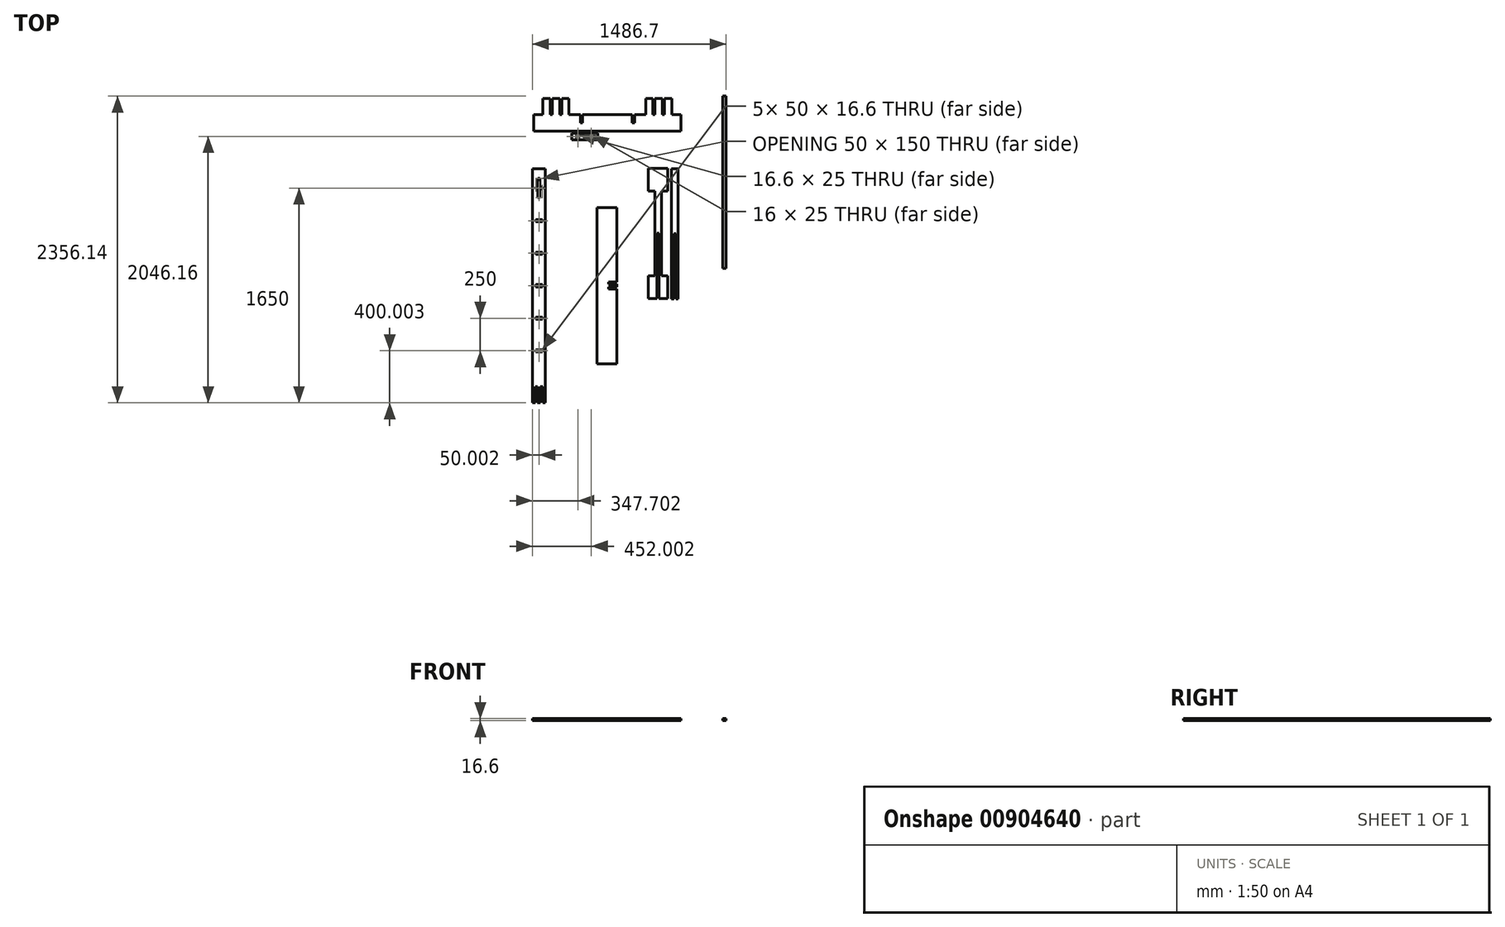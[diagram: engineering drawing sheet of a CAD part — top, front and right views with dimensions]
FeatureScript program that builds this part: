
annotation { "Feature Type Name" : "Feature", "Feature Type Description" : "" }
export const myFeature = defineFeature(function(context is Context, id is Id, definition is map)
    precondition{}
    {
        {
            assignVariable(context, id + "F0", {"name" : "s", "anyValue" : 16.6});
        }
        {
            var Q0;
            Q0=qCreatedBy(makeId("Top.planeOp"),FACE);
            var sketch = newSketch(context, id + "F1", { "sketchPlane" : qUnion([Q0])});
            skLineSegment(sketch, "E0.bottom", {"start": v(575, 24) * mm, "end": v(-575, 24) * mm});
            skLineSegment(sketch, "E0.top", {"start": v(575, 2324) * mm, "end": v(-575, 2324) * mm});
            skLineSegment(sketch, "E0.left", {"start": v(575, 24) * mm, "end": v(575, 2324) * mm});
            skLineSegment(sketch, "E0.right", {"start": v(-575, 24) * mm, "end": v(-575, 2324) * mm});
            skPoint(sketch, "E0.middle", {"position": v(0, 1174) * mm});
            skLineSegment(sketch, "E1.bottom", {"start": v(1816.08, 2142.02) * mm, "end": v(1916.08, 2142.02) * mm});
            skLineSegment(sketch, "E1.top", {"start": v(1816.08, 342.02) * mm, "end": v(1838.35, 342.02) * mm});
            skLineSegment(sketch, "E1.left", {"start": v(1816.08, 2142.02) * mm, "end": v(1816.08, 342.02) * mm});
            skLineSegment(sketch, "E1.right", {"start": v(1916.08, 2142.02) * mm, "end": v(1916.08, 342.02) * mm});
            skPoint(sketch, "E1.middle", {"position": v(1866.08, 1242.02) * mm});
            skLineSegment(sketch, "E2.top", {"start": v(1838.35, 467.02) * mm, "end": v(1854.95, 467.02) * mm});
            skLineSegment(sketch, "E2.left", {"start": v(1838.35, 342.02) * mm, "end": v(1838.35, 467.02) * mm});
            skLineSegment(sketch, "E2.right", {"start": v(1854.95, 342.02) * mm, "end": v(1854.95, 467.02) * mm});
            skLineSegment(sketch, "E3.top", {"start": v(1877.22, 467.02) * mm, "end": v(1893.82, 467.02) * mm});
            skLineSegment(sketch, "E3.left", {"start": v(1877.22, 342.02) * mm, "end": v(1877.22, 467.02) * mm});
            skLineSegment(sketch, "E3.right", {"start": v(1893.82, 342.02) * mm, "end": v(1893.82, 467.02) * mm});
            skLineSegment(sketch, "E4.trimOffspring", {"start": v(1854.95, 342.02) * mm, "end": v(1877.22, 342.02) * mm});
            skLineSegment(sketch, "E5.trimOffspring", {"start": v(1893.82, 342.02) * mm, "end": v(1916.08, 342.02) * mm});
            skLineSegment(sketch, "E6.bottom", {"start": v(1891.08, 1233.72) * mm, "end": v(1841.08, 1233.72) * mm});
            skLineSegment(sketch, "E6.top", {"start": v(1891.08, 1250.32) * mm, "end": v(1841.08, 1250.32) * mm});
            skLineSegment(sketch, "E6.left", {"start": v(1891.08, 1233.72) * mm, "end": v(1891.08, 1250.32) * mm});
            skLineSegment(sketch, "E6.right", {"start": v(1841.08, 1233.72) * mm, "end": v(1841.08, 1250.32) * mm});
            skLineSegment(sketch, "E7.0.1.0", {"start": v(1891.08, 1500.32) * mm, "end": v(1841.08, 1500.32) * mm});
            skLineSegment(sketch, "E7.0.1.1", {"start": v(1891.08, 1483.72) * mm, "end": v(1891.08, 1500.32) * mm});
            skPoint(sketch, "E7.0.1.2", {"position": v(1866.08, 1492.02) * mm});
            skLineSegment(sketch, "E7.0.1.3", {"start": v(1891.08, 1483.72) * mm, "end": v(1841.08, 1483.72) * mm});
            skLineSegment(sketch, "E7.0.1.4", {"start": v(1841.08, 1483.72) * mm, "end": v(1841.08, 1500.32) * mm});
            skPoint(sketch, "E7.0.1.5", {"position": v(1866.08, 1492.02) * mm});
            skLineSegment(sketch, "E7.direction1", {"start": v(1841.08, 1233.72) * mm, "end": v(1866.08, 1233.72) * mm, "construction": true});
            skLineSegment(sketch, "E7.direction2", {"start": v(1841.08, 1233.72) * mm, "end": v(1841.08, 1483.72) * mm, "construction": true});
            skLineSegment(sketch, "E8.0.0.2", {"start": v(1891.08, 1750.32) * mm, "end": v(1841.08, 1750.32) * mm});
            skLineSegment(sketch, "E8.3.0.2", {"start": v(1891.08, 1733.72) * mm, "end": v(1891.08, 1750.32) * mm});
            skPoint(sketch, "E8.6.0.2", {"position": v(1866.08, 1742.02) * mm});
            skLineSegment(sketch, "E8.7.0.2", {"start": v(1891.08, 1733.72) * mm, "end": v(1841.08, 1733.72) * mm});
            skLineSegment(sketch, "E8.10.0.2", {"start": v(1841.08, 1733.72) * mm, "end": v(1841.08, 1750.32) * mm});
            skPoint(sketch, "E8.13.0.2", {"position": v(1866.08, 1742.02) * mm});
            skLineSegment(sketch, "E8.0.0.3", {"start": v(1891.08, 2000.32) * mm, "end": v(1874.38, 2000.32) * mm});
            skLineSegment(sketch, "E8.3.0.3", {"start": v(1891.08, 1983.72) * mm, "end": v(1891.08, 2000.32) * mm});
            skPoint(sketch, "E8.6.0.3", {"position": v(1866.08, 1992.02) * mm});
            skLineSegment(sketch, "E8.7.0.3", {"start": v(1891.08, 1983.72) * mm, "end": v(1874.38, 1983.72) * mm});
            skLineSegment(sketch, "E8.10.0.3", {"start": v(1841.08, 1983.72) * mm, "end": v(1841.08, 2000.32) * mm});
            skPoint(sketch, "E8.13.0.3", {"position": v(1866.08, 1992.02) * mm});
            skLineSegment(sketch, "E9.0.1.0", {"start": v(1891.08, 983.72) * mm, "end": v(1841.08, 983.72) * mm});
            skPoint(sketch, "E9.0.1.1", {"position": v(1866.08, 992.02) * mm});
            skLineSegment(sketch, "E9.0.1.2", {"start": v(1891.08, 1000.32) * mm, "end": v(1841.08, 1000.32) * mm});
            skLineSegment(sketch, "E9.0.1.3", {"start": v(1841.08, 983.72) * mm, "end": v(1841.08, 1000.32) * mm});
            skLineSegment(sketch, "E9.0.1.4", {"start": v(1841.08, 983.72) * mm, "end": v(1866.08, 983.72) * mm, "construction": true});
            skLineSegment(sketch, "E9.0.1.5", {"start": v(1891.08, 983.72) * mm, "end": v(1891.08, 1000.32) * mm});
            skPoint(sketch, "E9.0.1.6", {"position": v(1866.08, 992.02) * mm});
            skLineSegment(sketch, "E9.direction2", {"start": v(1841.08, 1233.72) * mm, "end": v(1841.08, 983.72) * mm, "construction": true});
            skLineSegment(sketch, "E10.0.0.2", {"start": v(1891.08, 733.72) * mm, "end": v(1841.08, 733.72) * mm});
            skPoint(sketch, "E10.3.0.2", {"position": v(1866.08, 742.02) * mm});
            skLineSegment(sketch, "E10.4.0.2", {"start": v(1891.08, 750.32) * mm, "end": v(1841.08, 750.32) * mm});
            skLineSegment(sketch, "E10.7.0.2", {"start": v(1841.08, 733.72) * mm, "end": v(1841.08, 750.32) * mm});
            skLineSegment(sketch, "E10.10.0.2", {"start": v(1841.08, 733.72) * mm, "end": v(1866.08, 733.72) * mm, "construction": true});
            skLineSegment(sketch, "E10.13.0.2", {"start": v(1891.08, 733.72) * mm, "end": v(1891.08, 750.32) * mm});
            skPoint(sketch, "E10.16.0.2", {"position": v(1866.08, 742.02) * mm});
            skPoint(sketch, "E11.1.0.0", {"position": v(1991.08, 1242.02) * mm});
            skPoint(sketch, "E11.1.0.1", {"position": v(1991.08, 742.02) * mm});
            skPoint(sketch, "E11.1.0.2", {"position": v(1991.08, 1742.02) * mm});
            skLineSegment(sketch, "E11.1.0.3", {"start": v(1941.08, 2142.02) * mm, "end": v(1941.08, 342.02) * mm});
            skPoint(sketch, "E11.1.0.4", {"position": v(1991.08, 1492.02) * mm});
            skPoint(sketch, "E11.1.0.5", {"position": v(1991.08, 1992.02) * mm});
            skPoint(sketch, "E11.1.0.6", {"position": v(1991.08, 992.02) * mm});
            skLineSegment(sketch, "E11.1.0.7", {"start": v(1966.08, 1233.72) * mm, "end": v(1966.08, 1483.72) * mm, "construction": true});
            skLineSegment(sketch, "E11.1.0.8", {"start": v(2041.08, 2142.02) * mm, "end": v(2041.08, 342.02) * mm});
            skLineSegment(sketch, "E11.1.0.9", {"start": v(1941.08, 2142.02) * mm, "end": v(2041.08, 2142.02) * mm});
            skPoint(sketch, "E11.1.0.10", {"position": v(1991.08, 1992.02) * mm});
            skLineSegment(sketch, "E11.1.0.11", {"start": v(1966.08, 1233.72) * mm, "end": v(1966.08, 983.72) * mm, "construction": true});
            skPoint(sketch, "E11.1.0.12", {"position": v(1991.08, 1242.02) * mm});
            skPoint(sketch, "E11.1.0.13", {"position": v(1991.08, 1492.02) * mm});
            skPoint(sketch, "E11.1.0.14", {"position": v(1991.08, 992.02) * mm});
            skLineSegment(sketch, "E11.1.0.15", {"start": v(2018.82, 342.02) * mm, "end": v(2018.82, 467.02) * mm});
            skLineSegment(sketch, "E11.1.0.16", {"start": v(1979.95, 342.02) * mm, "end": v(1979.95, 467.02) * mm});
            skPoint(sketch, "E11.1.0.17", {"position": v(1991.08, 1742.02) * mm});
            skLineSegment(sketch, "E11.1.0.18", {"start": v(1963.35, 342.02) * mm, "end": v(1963.35, 467.02) * mm});
            skLineSegment(sketch, "E11.1.0.19", {"start": v(2002.22, 342.02) * mm, "end": v(2002.22, 467.02) * mm});
            skPoint(sketch, "E11.1.0.20", {"position": v(1991.08, 742.02) * mm});
            skLineSegment(sketch, "E11.1.0.21", {"start": v(2016.08, 1500.32) * mm, "end": v(1966.08, 1500.32) * mm});
            skLineSegment(sketch, "E11.1.0.22", {"start": v(2016.08, 2000.32) * mm, "end": v(1966.08, 2000.32) * mm});
            skLineSegment(sketch, "E11.1.0.23", {"start": v(2016.08, 1983.72) * mm, "end": v(1966.08, 1983.72) * mm});
            skLineSegment(sketch, "E11.1.0.24", {"start": v(2016.08, 1483.72) * mm, "end": v(1966.08, 1483.72) * mm});
            skLineSegment(sketch, "E11.1.0.25", {"start": v(2016.08, 1483.72) * mm, "end": v(2016.08, 1500.32) * mm});
            skLineSegment(sketch, "E11.1.0.26", {"start": v(2016.08, 1983.72) * mm, "end": v(2016.08, 2000.32) * mm});
            skLineSegment(sketch, "E11.1.0.27", {"start": v(1966.08, 1983.72) * mm, "end": v(1966.08, 2000.32) * mm});
            skLineSegment(sketch, "E11.1.0.28", {"start": v(2016.08, 1733.72) * mm, "end": v(2016.08, 1750.32) * mm});
            skLineSegment(sketch, "E11.1.0.29", {"start": v(1941.08, 342.02) * mm, "end": v(1963.35, 342.02) * mm});
            skLineSegment(sketch, "E11.1.0.30", {"start": v(1979.95, 342.02) * mm, "end": v(2002.22, 342.02) * mm});
            skLineSegment(sketch, "E11.1.0.31", {"start": v(2016.08, 983.72) * mm, "end": v(1966.08, 983.72) * mm});
            skLineSegment(sketch, "E11.1.0.32", {"start": v(2016.08, 1750.32) * mm, "end": v(1966.08, 1750.32) * mm});
            skLineSegment(sketch, "E11.1.0.33", {"start": v(1963.35, 467.02) * mm, "end": v(1979.95, 467.02) * mm});
            skLineSegment(sketch, "E11.1.0.34", {"start": v(2016.08, 1000.32) * mm, "end": v(1966.08, 1000.32) * mm});
            skLineSegment(sketch, "E11.1.0.35", {"start": v(2016.08, 983.72) * mm, "end": v(2016.08, 1000.32) * mm});
            skLineSegment(sketch, "E11.1.0.36", {"start": v(1966.08, 1483.72) * mm, "end": v(1966.08, 1500.32) * mm});
            skLineSegment(sketch, "E11.1.0.37", {"start": v(2018.82, 342.02) * mm, "end": v(2041.08, 342.02) * mm});
            skLineSegment(sketch, "E11.1.0.38", {"start": v(1966.08, 733.72) * mm, "end": v(1966.08, 750.32) * mm});
            skLineSegment(sketch, "E11.1.0.39", {"start": v(2002.22, 467.02) * mm, "end": v(2018.82, 467.02) * mm});
            skLineSegment(sketch, "E11.1.0.40", {"start": v(2016.08, 1733.72) * mm, "end": v(1966.08, 1733.72) * mm});
            skLineSegment(sketch, "E11.1.0.41", {"start": v(1966.08, 733.72) * mm, "end": v(1991.08, 733.72) * mm, "construction": true});
            skLineSegment(sketch, "E11.1.0.42", {"start": v(2016.08, 1233.72) * mm, "end": v(2016.08, 1250.32) * mm});
            skLineSegment(sketch, "E11.1.0.43", {"start": v(1966.08, 983.72) * mm, "end": v(1966.08, 1000.32) * mm});
            skLineSegment(sketch, "E11.1.0.44", {"start": v(1966.08, 1733.72) * mm, "end": v(1966.08, 1750.32) * mm});
            skLineSegment(sketch, "E11.1.0.45", {"start": v(1966.08, 983.72) * mm, "end": v(1991.08, 983.72) * mm, "construction": true});
            skLineSegment(sketch, "E11.1.0.46", {"start": v(2016.08, 733.72) * mm, "end": v(1966.08, 733.72) * mm});
            skLineSegment(sketch, "E11.1.0.47", {"start": v(2016.08, 1233.72) * mm, "end": v(1966.08, 1233.72) * mm});
            skLineSegment(sketch, "E11.1.0.48", {"start": v(2016.08, 733.72) * mm, "end": v(2016.08, 750.32) * mm});
            skLineSegment(sketch, "E11.1.0.49", {"start": v(2016.08, 750.32) * mm, "end": v(1966.08, 750.32) * mm});
            skLineSegment(sketch, "E11.1.0.50", {"start": v(2016.08, 1250.32) * mm, "end": v(1966.08, 1250.32) * mm});
            skLineSegment(sketch, "E11.1.0.51", {"start": v(1966.08, 1233.72) * mm, "end": v(1966.08, 1250.32) * mm});
            skLineSegment(sketch, "E11.1.0.52", {"start": v(1966.08, 1233.72) * mm, "end": v(1991.08, 1233.72) * mm, "construction": true});
            skLineSegment(sketch, "E11.1.0.53", {"start": v(1966.08, 1233.72) * mm, "end": v(1991.08, 1233.72) * mm, "construction": true});
            skPoint(sketch, "E11.2.0.0", {"position": v(2116.08, 1242.02) * mm});
            skPoint(sketch, "E11.2.0.1", {"position": v(2116.08, 742.02) * mm});
            skPoint(sketch, "E11.2.0.2", {"position": v(2116.08, 1742.02) * mm});
            skLineSegment(sketch, "E11.2.0.3", {"start": v(2066.08, 2142.02) * mm, "end": v(2066.08, 342.02) * mm});
            skPoint(sketch, "E11.2.0.4", {"position": v(2116.08, 1492.02) * mm});
            skPoint(sketch, "E11.2.0.5", {"position": v(2116.08, 1992.02) * mm});
            skPoint(sketch, "E11.2.0.6", {"position": v(2116.08, 992.02) * mm});
            skLineSegment(sketch, "E11.2.0.7", {"start": v(2091.08, 1233.72) * mm, "end": v(2091.08, 1483.72) * mm, "construction": true});
            skLineSegment(sketch, "E11.2.0.8", {"start": v(2166.08, 2142.02) * mm, "end": v(2166.08, 342.02) * mm});
            skLineSegment(sketch, "E11.2.0.9", {"start": v(2066.08, 2142.02) * mm, "end": v(2166.08, 2142.02) * mm});
            skPoint(sketch, "E11.2.0.10", {"position": v(2116.08, 1992.02) * mm});
            skLineSegment(sketch, "E11.2.0.11", {"start": v(2091.08, 1233.72) * mm, "end": v(2091.08, 983.72) * mm, "construction": true});
            skPoint(sketch, "E11.2.0.12", {"position": v(2116.08, 1242.02) * mm});
            skPoint(sketch, "E11.2.0.13", {"position": v(2116.08, 1492.02) * mm});
            skPoint(sketch, "E11.2.0.14", {"position": v(2116.08, 992.02) * mm});
            skLineSegment(sketch, "E11.2.0.15", {"start": v(2143.82, 342.02) * mm, "end": v(2143.82, 467.02) * mm});
            skLineSegment(sketch, "E11.2.0.16", {"start": v(2104.95, 342.02) * mm, "end": v(2104.95, 467.02) * mm});
            skPoint(sketch, "E11.2.0.17", {"position": v(2116.08, 1742.02) * mm});
            skLineSegment(sketch, "E11.2.0.18", {"start": v(2088.35, 342.02) * mm, "end": v(2088.35, 467.02) * mm});
            skLineSegment(sketch, "E11.2.0.19", {"start": v(2127.22, 342.02) * mm, "end": v(2127.22, 467.02) * mm});
            skPoint(sketch, "E11.2.0.20", {"position": v(2116.08, 742.02) * mm});
            skLineSegment(sketch, "E11.2.0.21", {"start": v(2141.08, 1500.32) * mm, "end": v(2091.08, 1500.32) * mm});
            skLineSegment(sketch, "E11.2.0.22", {"start": v(2141.08, 2000.32) * mm, "end": v(2091.08, 2000.32) * mm});
            skLineSegment(sketch, "E11.2.0.23", {"start": v(2141.08, 1983.72) * mm, "end": v(2091.08, 1983.72) * mm});
            skLineSegment(sketch, "E11.2.0.24", {"start": v(2141.08, 1483.72) * mm, "end": v(2091.08, 1483.72) * mm});
            skLineSegment(sketch, "E11.2.0.25", {"start": v(2141.08, 1483.72) * mm, "end": v(2141.08, 1500.32) * mm});
            skLineSegment(sketch, "E11.2.0.26", {"start": v(2141.08, 1983.72) * mm, "end": v(2141.08, 2000.32) * mm});
            skLineSegment(sketch, "E11.2.0.27", {"start": v(2091.08, 1983.72) * mm, "end": v(2091.08, 2000.32) * mm});
            skLineSegment(sketch, "E11.2.0.28", {"start": v(2141.08, 1733.72) * mm, "end": v(2141.08, 1750.32) * mm});
            skLineSegment(sketch, "E11.2.0.29", {"start": v(2066.08, 342.02) * mm, "end": v(2088.35, 342.02) * mm});
            skLineSegment(sketch, "E11.2.0.30", {"start": v(2104.95, 342.02) * mm, "end": v(2127.22, 342.02) * mm});
            skLineSegment(sketch, "E11.2.0.31", {"start": v(2141.08, 983.72) * mm, "end": v(2091.08, 983.72) * mm});
            skLineSegment(sketch, "E11.2.0.32", {"start": v(2141.08, 1750.32) * mm, "end": v(2091.08, 1750.32) * mm});
            skLineSegment(sketch, "E11.2.0.33", {"start": v(2088.35, 467.02) * mm, "end": v(2104.95, 467.02) * mm});
            skLineSegment(sketch, "E11.2.0.34", {"start": v(2141.08, 1000.32) * mm, "end": v(2091.08, 1000.32) * mm});
            skLineSegment(sketch, "E11.2.0.35", {"start": v(2141.08, 983.72) * mm, "end": v(2141.08, 1000.32) * mm});
            skLineSegment(sketch, "E11.2.0.36", {"start": v(2091.08, 1483.72) * mm, "end": v(2091.08, 1500.32) * mm});
            skLineSegment(sketch, "E11.2.0.37", {"start": v(2143.82, 342.02) * mm, "end": v(2166.08, 342.02) * mm});
            skLineSegment(sketch, "E11.2.0.38", {"start": v(2091.08, 733.72) * mm, "end": v(2091.08, 750.32) * mm});
            skLineSegment(sketch, "E11.2.0.39", {"start": v(2127.22, 467.02) * mm, "end": v(2143.82, 467.02) * mm});
            skLineSegment(sketch, "E11.2.0.40", {"start": v(2141.08, 1733.72) * mm, "end": v(2091.08, 1733.72) * mm});
            skLineSegment(sketch, "E11.2.0.41", {"start": v(2091.08, 733.72) * mm, "end": v(2116.08, 733.72) * mm, "construction": true});
            skLineSegment(sketch, "E11.2.0.42", {"start": v(2141.08, 1233.72) * mm, "end": v(2141.08, 1250.32) * mm});
            skLineSegment(sketch, "E11.2.0.43", {"start": v(2091.08, 983.72) * mm, "end": v(2091.08, 1000.32) * mm});
            skLineSegment(sketch, "E11.2.0.44", {"start": v(2091.08, 1733.72) * mm, "end": v(2091.08, 1750.32) * mm});
            skLineSegment(sketch, "E11.2.0.45", {"start": v(2091.08, 983.72) * mm, "end": v(2116.08, 983.72) * mm, "construction": true});
            skLineSegment(sketch, "E11.2.0.46", {"start": v(2141.08, 733.72) * mm, "end": v(2091.08, 733.72) * mm});
            skLineSegment(sketch, "E11.2.0.47", {"start": v(2141.08, 1233.72) * mm, "end": v(2091.08, 1233.72) * mm});
            skLineSegment(sketch, "E11.2.0.48", {"start": v(2141.08, 733.72) * mm, "end": v(2141.08, 750.32) * mm});
            skLineSegment(sketch, "E11.2.0.49", {"start": v(2141.08, 750.32) * mm, "end": v(2091.08, 750.32) * mm});
            skLineSegment(sketch, "E11.2.0.50", {"start": v(2141.08, 1250.32) * mm, "end": v(2091.08, 1250.32) * mm});
            skLineSegment(sketch, "E11.2.0.51", {"start": v(2091.08, 1233.72) * mm, "end": v(2091.08, 1250.32) * mm});
            skLineSegment(sketch, "E11.2.0.52", {"start": v(2091.08, 1233.72) * mm, "end": v(2116.08, 1233.72) * mm, "construction": true});
            skLineSegment(sketch, "E11.2.0.53", {"start": v(2091.08, 1233.72) * mm, "end": v(2116.08, 1233.72) * mm, "construction": true});
            skLineSegment(sketch, "E11.direction1", {"start": v(1816.08, 342.02) * mm, "end": v(1941.08, 342.02) * mm, "construction": true});
            skPoint(sketch, "E12.0.3.0", {"position": v(2241.08, 1242.02) * mm});
            skPoint(sketch, "E12.1.3.0", {"position": v(2241.08, 742.02) * mm});
            skPoint(sketch, "E12.2.3.0", {"position": v(2241.08, 1742.02) * mm});
            skLineSegment(sketch, "E12.3.3.0", {"start": v(2191.08, 2142.02) * mm, "end": v(2191.08, 342.02) * mm});
            skPoint(sketch, "E12.6.3.0", {"position": v(2241.08, 1492.02) * mm});
            skPoint(sketch, "E12.7.3.0", {"position": v(2241.08, 1992.02) * mm});
            skPoint(sketch, "E12.8.3.0", {"position": v(2241.08, 992.02) * mm});
            skLineSegment(sketch, "E12.9.3.0", {"start": v(2216.08, 1233.72) * mm, "end": v(2216.08, 1483.72) * mm, "construction": true});
            skLineSegment(sketch, "E12.12.3.0", {"start": v(2291.08, 2142.02) * mm, "end": v(2291.08, 342.02) * mm});
            skLineSegment(sketch, "E12.15.3.0", {"start": v(2191.08, 2142.02) * mm, "end": v(2291.08, 2142.02) * mm});
            skPoint(sketch, "E12.18.3.0", {"position": v(2241.08, 1992.02) * mm});
            skLineSegment(sketch, "E12.19.3.0", {"start": v(2216.08, 1233.72) * mm, "end": v(2216.08, 983.72) * mm, "construction": true});
            skPoint(sketch, "E12.22.3.0", {"position": v(2241.08, 1242.02) * mm});
            skPoint(sketch, "E12.23.3.0", {"position": v(2241.08, 1492.02) * mm});
            skPoint(sketch, "E12.24.3.0", {"position": v(2241.08, 992.02) * mm});
            skLineSegment(sketch, "E12.25.3.0", {"start": v(2268.82, 342.02) * mm, "end": v(2268.82, 467.02) * mm});
            skLineSegment(sketch, "E12.28.3.0", {"start": v(2229.95, 342.02) * mm, "end": v(2229.95, 467.02) * mm});
            skPoint(sketch, "E12.31.3.0", {"position": v(2241.08, 1742.02) * mm});
            skLineSegment(sketch, "E12.32.3.0", {"start": v(2213.35, 342.02) * mm, "end": v(2213.35, 467.02) * mm});
            skLineSegment(sketch, "E12.35.3.0", {"start": v(2252.22, 342.02) * mm, "end": v(2252.22, 467.02) * mm});
            skPoint(sketch, "E12.38.3.0", {"position": v(2241.08, 742.02) * mm});
            skLineSegment(sketch, "E12.39.3.0", {"start": v(2266.08, 1500.32) * mm, "end": v(2216.08, 1500.32) * mm});
            skLineSegment(sketch, "E12.42.3.0", {"start": v(2266.08, 2000.32) * mm, "end": v(2216.08, 2000.32) * mm});
            skLineSegment(sketch, "E12.45.3.0", {"start": v(2266.08, 1983.72) * mm, "end": v(2216.08, 1983.72) * mm});
            skLineSegment(sketch, "E12.48.3.0", {"start": v(2266.08, 1483.72) * mm, "end": v(2216.08, 1483.72) * mm});
            skLineSegment(sketch, "E12.51.3.0", {"start": v(2266.08, 1483.72) * mm, "end": v(2266.08, 1500.32) * mm});
            skLineSegment(sketch, "E12.54.3.0", {"start": v(2266.08, 1983.72) * mm, "end": v(2266.08, 2000.32) * mm});
            skLineSegment(sketch, "E12.57.3.0", {"start": v(2216.08, 1983.72) * mm, "end": v(2216.08, 2000.32) * mm});
            skLineSegment(sketch, "E12.60.3.0", {"start": v(2266.08, 1733.72) * mm, "end": v(2266.08, 1750.32) * mm});
            skLineSegment(sketch, "E12.63.3.0", {"start": v(2191.08, 342.02) * mm, "end": v(2213.35, 342.02) * mm});
            skLineSegment(sketch, "E12.66.3.0", {"start": v(2229.95, 342.02) * mm, "end": v(2252.22, 342.02) * mm});
            skLineSegment(sketch, "E12.69.3.0", {"start": v(2266.08, 983.72) * mm, "end": v(2216.08, 983.72) * mm});
            skLineSegment(sketch, "E12.72.3.0", {"start": v(2266.08, 1750.32) * mm, "end": v(2216.08, 1750.32) * mm});
            skLineSegment(sketch, "E12.75.3.0", {"start": v(2213.35, 467.02) * mm, "end": v(2229.95, 467.02) * mm});
            skLineSegment(sketch, "E12.78.3.0", {"start": v(2266.08, 1000.32) * mm, "end": v(2216.08, 1000.32) * mm});
            skLineSegment(sketch, "E12.81.3.0", {"start": v(2266.08, 983.72) * mm, "end": v(2266.08, 1000.32) * mm});
            skLineSegment(sketch, "E12.84.3.0", {"start": v(2216.08, 1483.72) * mm, "end": v(2216.08, 1500.32) * mm});
            skLineSegment(sketch, "E12.87.3.0", {"start": v(2268.82, 342.02) * mm, "end": v(2291.08, 342.02) * mm});
            skLineSegment(sketch, "E12.90.3.0", {"start": v(2216.08, 733.72) * mm, "end": v(2216.08, 750.32) * mm});
            skLineSegment(sketch, "E12.93.3.0", {"start": v(2252.22, 467.02) * mm, "end": v(2268.82, 467.02) * mm});
            skLineSegment(sketch, "E12.96.3.0", {"start": v(2266.08, 1733.72) * mm, "end": v(2216.08, 1733.72) * mm});
            skLineSegment(sketch, "E12.99.3.0", {"start": v(2216.08, 733.72) * mm, "end": v(2241.08, 733.72) * mm, "construction": true});
            skLineSegment(sketch, "E12.102.3.0", {"start": v(2266.08, 1233.72) * mm, "end": v(2266.08, 1250.32) * mm});
            skLineSegment(sketch, "E12.105.3.0", {"start": v(2216.08, 983.72) * mm, "end": v(2216.08, 1000.32) * mm});
            skLineSegment(sketch, "E12.108.3.0", {"start": v(2216.08, 1733.72) * mm, "end": v(2216.08, 1750.32) * mm});
            skLineSegment(sketch, "E12.111.3.0", {"start": v(2216.08, 983.72) * mm, "end": v(2241.08, 983.72) * mm, "construction": true});
            skLineSegment(sketch, "E12.114.3.0", {"start": v(2266.08, 733.72) * mm, "end": v(2216.08, 733.72) * mm});
            skLineSegment(sketch, "E12.117.3.0", {"start": v(2266.08, 1233.72) * mm, "end": v(2216.08, 1233.72) * mm});
            skLineSegment(sketch, "E12.120.3.0", {"start": v(2266.08, 733.72) * mm, "end": v(2266.08, 750.32) * mm});
            skLineSegment(sketch, "E12.123.3.0", {"start": v(2266.08, 750.32) * mm, "end": v(2216.08, 750.32) * mm});
            skLineSegment(sketch, "E12.126.3.0", {"start": v(2266.08, 1250.32) * mm, "end": v(2216.08, 1250.32) * mm});
            skLineSegment(sketch, "E12.129.3.0", {"start": v(2216.08, 1233.72) * mm, "end": v(2216.08, 1250.32) * mm});
            skLineSegment(sketch, "E12.132.3.0", {"start": v(2216.08, 1233.72) * mm, "end": v(2241.08, 1233.72) * mm, "construction": true});
            skLineSegment(sketch, "E12.135.3.0", {"start": v(2216.08, 1233.72) * mm, "end": v(2241.08, 1233.72) * mm, "construction": true});
            skLineSegment(sketch, "E13.right", {"start": v(1815.82, 2164.49) * mm, "end": v(1815.82, 2289.49) * mm});
            skLineSegment(sketch, "E14.top", {"start": v(1896.82, 2414.49) * mm, "end": v(1952.42, 2414.49) * mm});
            skLineSegment(sketch, "E14.left", {"start": v(1896.82, 2289.49) * mm, "end": v(1896.82, 2414.49) * mm});
            skLineSegment(sketch, "E14.right", {"start": v(2096.82, 2289.49) * mm, "end": v(2096.82, 2414.49) * mm});
            skLineSegment(sketch, "E15.trimOffspring", {"start": v(1896.82, 2289.49) * mm, "end": v(1815.82, 2289.49) * mm});
            skLineSegment(sketch, "E16.trimOffspring", {"start": v(2390.82, 2289.49) * mm, "end": v(2096.82, 2289.49) * mm});
            skLineSegment(sketch, "E17.top", {"start": v(1952.42, 2356.68) * mm, "end": v(1969.02, 2356.68) * mm});
            skLineSegment(sketch, "E17.left", {"start": v(1952.42, 2414.49) * mm, "end": v(1952.42, 2356.68) * mm});
            skLineSegment(sketch, "E17.right", {"start": v(1969.02, 2414.49) * mm, "end": v(1969.02, 2356.68) * mm});
            skLineSegment(sketch, "E18.top", {"start": v(2024.62, 2357.18) * mm, "end": v(2041.22, 2357.18) * mm});
            skLineSegment(sketch, "E18.left", {"start": v(2024.62, 2414.49) * mm, "end": v(2024.62, 2357.18) * mm});
            skLineSegment(sketch, "E18.right", {"start": v(2041.22, 2414.49) * mm, "end": v(2041.22, 2357.18) * mm});
            skLineSegment(sketch, "E19.trimOffspring", {"start": v(1969.02, 2414.49) * mm, "end": v(2024.62, 2414.49) * mm});
            skLineSegment(sketch, "E20.trimOffspring", {"start": v(2041.22, 2414.49) * mm, "end": v(2096.82, 2414.49) * mm});
            skLineSegment(sketch, "E21.MirrorCS", {"start": v(2829.22, 2356.68) * mm, "end": v(2813.22, 2356.68) * mm});
            skLineSegment(sketch, "E22.MirrorCS", {"start": v(2757.22, 2357.18) * mm, "end": v(2741.22, 2357.18) * mm});
            skLineSegment(sketch, "E23.MirrorCS", {"start": v(2885.22, 2414.49) * mm, "end": v(2829.22, 2414.49) * mm});
            skLineSegment(sketch, "E24.MirrorCS", {"start": v(2829.22, 2414.49) * mm, "end": v(2829.22, 2356.68) * mm});
            skLineSegment(sketch, "E25.MirrorCS", {"start": v(2885.22, 2289.49) * mm, "end": v(2885.22, 2414.49) * mm});
            skLineSegment(sketch, "E26.MirrorCS", {"start": v(2391.22, 2289.49) * mm, "end": v(2685.22, 2289.49) * mm});
            skLineSegment(sketch, "E27.MirrorCS", {"start": v(2757.22, 2414.49) * mm, "end": v(2757.22, 2357.18) * mm});
            skLineSegment(sketch, "E28.MirrorCS", {"start": v(2813.22, 2414.49) * mm, "end": v(2813.22, 2356.68) * mm});
            skLineSegment(sketch, "E29.MirrorCS", {"start": v(2885.22, 2289.49) * mm, "end": v(2966.22, 2289.49) * mm});
            skLineSegment(sketch, "E30.MirrorCS", {"start": v(2741.22, 2414.49) * mm, "end": v(2741.22, 2357.18) * mm});
            skLineSegment(sketch, "E31.MirrorCS", {"start": v(2813.22, 2414.49) * mm, "end": v(2757.22, 2414.49) * mm});
            skLineSegment(sketch, "E32.MirrorCS", {"start": v(2685.22, 2289.49) * mm, "end": v(2685.22, 2414.49) * mm});
            skLineSegment(sketch, "E33.MirrorCS", {"start": v(2966.22, 2164.49) * mm, "end": v(2966.22, 2289.49) * mm});
            skLineSegment(sketch, "E34.MirrorCS", {"start": v(2741.22, 2414.49) * mm, "end": v(2685.22, 2414.49) * mm});
            skLineSegment(sketch, "E35", {"start": v(2966.22, 2164.49) * mm, "end": v(1815.82, 2164.49) * mm});
            skLineSegment(sketch, "E36.right", {"start": v(1826.82, 2429.9) * mm, "end": v(1826.82, 2554.9) * mm});
            skLineSegment(sketch, "E37.top", {"start": v(1896.82, 2679.9) * mm, "end": v(1952.42, 2679.9) * mm});
            skLineSegment(sketch, "E37.left", {"start": v(1896.82, 2554.9) * mm, "end": v(1896.82, 2679.9) * mm});
            skLineSegment(sketch, "E37.right", {"start": v(2096.82, 2554.9) * mm, "end": v(2096.82, 2679.9) * mm});
            skLineSegment(sketch, "E38.trimOffspring", {"start": v(1896.82, 2554.9) * mm, "end": v(1826.82, 2554.9) * mm});
            skLineSegment(sketch, "E39.top", {"start": v(1952.42, 2554.9) * mm, "end": v(1969.02, 2554.9) * mm});
            skLineSegment(sketch, "E39.left", {"start": v(1952.42, 2679.9) * mm, "end": v(1952.42, 2554.9) * mm});
            skLineSegment(sketch, "E39.right", {"start": v(1969.02, 2679.9) * mm, "end": v(1969.02, 2554.9) * mm});
            skLineSegment(sketch, "E40.top", {"start": v(2024.62, 2554.9) * mm, "end": v(2041.22, 2554.9) * mm});
            skLineSegment(sketch, "E40.left", {"start": v(2024.62, 2679.9) * mm, "end": v(2024.62, 2554.9) * mm});
            skLineSegment(sketch, "E40.right", {"start": v(2041.22, 2679.9) * mm, "end": v(2041.22, 2554.9) * mm});
            skLineSegment(sketch, "E41.trimOffspring", {"start": v(1969.02, 2679.9) * mm, "end": v(2024.62, 2679.9) * mm});
            skLineSegment(sketch, "E42.trimOffspring", {"start": v(2041.22, 2679.9) * mm, "end": v(2096.82, 2679.9) * mm});
            skLineSegment(sketch, "E43.MirrorCS", {"start": v(2829.22, 2554.9) * mm, "end": v(2813.22, 2554.9) * mm});
            skLineSegment(sketch, "E44.MirrorCS", {"start": v(2757.22, 2554.9) * mm, "end": v(2741.22, 2554.9) * mm});
            skLineSegment(sketch, "E45.MirrorCS", {"start": v(2885.22, 2679.9) * mm, "end": v(2829.22, 2679.9) * mm});
            skLineSegment(sketch, "E46.MirrorCS", {"start": v(2829.22, 2679.9) * mm, "end": v(2829.22, 2554.9) * mm});
            skLineSegment(sketch, "E47.MirrorCS", {"start": v(2885.22, 2554.9) * mm, "end": v(2885.22, 2679.9) * mm});
            skLineSegment(sketch, "E48.MirrorCS", {"start": v(2757.22, 2679.9) * mm, "end": v(2757.22, 2554.9) * mm});
            skLineSegment(sketch, "E49.MirrorCS", {"start": v(2813.22, 2679.9) * mm, "end": v(2813.22, 2554.9) * mm});
            skLineSegment(sketch, "E50.MirrorCS", {"start": v(2885.22, 2554.9) * mm, "end": v(2955.22, 2554.9) * mm});
            skLineSegment(sketch, "E51.MirrorCS", {"start": v(2741.22, 2679.9) * mm, "end": v(2741.22, 2554.9) * mm});
            skLineSegment(sketch, "E52.MirrorCS", {"start": v(2813.22, 2679.9) * mm, "end": v(2757.22, 2679.9) * mm});
            skLineSegment(sketch, "E53.MirrorCS", {"start": v(2685.22, 2554.9) * mm, "end": v(2685.22, 2679.9) * mm});
            skLineSegment(sketch, "E54.MirrorCS", {"start": v(2955.22, 2429.9) * mm, "end": v(2955.22, 2554.9) * mm});
            skLineSegment(sketch, "E55.MirrorCS", {"start": v(2741.22, 2679.9) * mm, "end": v(2685.22, 2679.9) * mm});
            skLineSegment(sketch, "E56", {"start": v(2955.22, 2429.9) * mm, "end": v(1826.82, 2429.9) * mm});
            skLineSegment(sketch, "E57.bottom", {"start": v(1874.38, 1917.02) * mm, "end": v(1857.78, 1917.02) * mm});
            skLineSegment(sketch, "E57.top", {"start": v(1874.38, 2067.02) * mm, "end": v(1857.78, 2067.02) * mm});
            skLineSegment(sketch, "E57.left", {"start": v(1874.38, 1917.02) * mm, "end": v(1874.38, 1983.72) * mm});
            skLineSegment(sketch, "E57.right", {"start": v(1857.78, 1917.02) * mm, "end": v(1857.78, 1983.72) * mm});
            skLineSegment(sketch, "E58.bottom", {"start": v(2316.08, 2363.18) * mm, "end": v(2116.08, 2363.18) * mm});
            skLineSegment(sketch, "E58.top", {"start": v(2316.08, 2413.18) * mm, "end": v(2116.08, 2413.18) * mm});
            skLineSegment(sketch, "E58.left", {"start": v(2316.08, 2363.18) * mm, "end": v(2316.08, 2413.18) * mm});
            skLineSegment(sketch, "E58.right", {"start": v(2116.08, 2363.18) * mm, "end": v(2116.08, 2413.18) * mm});
            skPoint(sketch, "E58.middle", {"position": v(2216.08, 2388.18) * mm});
            skLineSegment(sketch, "E59.bottom", {"start": v(2155.48, 2375.68) * mm, "end": v(2172.08, 2375.68) * mm});
            skLineSegment(sketch, "E59.top", {"start": v(2155.48, 2400.68) * mm, "end": v(2172.08, 2400.68) * mm});
            skLineSegment(sketch, "E59.left", {"start": v(2155.48, 2375.68) * mm, "end": v(2155.48, 2400.68) * mm});
            skLineSegment(sketch, "E59.right", {"start": v(2172.08, 2375.68) * mm, "end": v(2172.08, 2400.68) * mm});
            skPoint(sketch, "E59.middle", {"position": v(2163.78, 2388.18) * mm});
            skLineSegment(sketch, "E60.MirrorCS", {"start": v(2276.08, 2400.68) * mm, "end": v(2260.08, 2400.68) * mm});
            skLineSegment(sketch, "E61.MirrorCS", {"start": v(2276.08, 2375.68) * mm, "end": v(2276.08, 2400.68) * mm});
            skPoint(sketch, "E62.MirrorP", {"position": v(2252.08, 2388.18) * mm});
            skLineSegment(sketch, "E63.MirrorCS", {"start": v(2260.08, 2375.68) * mm, "end": v(2260.08, 2400.68) * mm});
            skLineSegment(sketch, "E64.MirrorCS", {"start": v(2276.08, 2375.68) * mm, "end": v(2260.08, 2375.68) * mm});
            skLineSegment(sketch, "E65.direction1", {"start": v(2116.08, 2363.18) * mm, "end": v(2332.18, 2363.18) * mm, "construction": true});
            skLineSegment(sketch, "E66.bottom", {"start": v(2312.23, 643.04) * mm, "end": v(2462.23, 643.04) * mm});
            skLineSegment(sketch, "E66.top", {"start": v(2312.23, 1843.04) * mm, "end": v(2462.23, 1843.04) * mm});
            skLineSegment(sketch, "E66.left", {"start": v(2312.23, 643.04) * mm, "end": v(2312.23, 1843.04) * mm});
            skLineSegment(sketch, "E66.right", {"start": v(2462.23, 643.04) * mm, "end": v(2462.23, 1215.09) * mm});
            skPoint(sketch, "E66.middle", {"position": v(2387.23, 1243.04) * mm});
            skLineSegment(sketch, "E67.bottom", {"start": v(2515.08, 643.04) * mm, "end": v(2690.08, 643.04) * mm});
            skLineSegment(sketch, "E67.top", {"start": v(2515.08, 2143.04) * mm, "end": v(2690.08, 2143.04) * mm});
            skLineSegment(sketch, "E67.left", {"start": v(2515.08, 643.04) * mm, "end": v(2515.08, 2143.04) * mm});
            skLineSegment(sketch, "E67.right", {"start": v(2690.08, 643.04) * mm, "end": v(2690.08, 2143.04) * mm});
            skPoint(sketch, "E67.middle", {"position": v(2602.58, 1393.04) * mm});
            skLineSegment(sketch, "E68.top", {"start": v(2855.02, 2143.67) * mm, "end": v(2705.02, 2143.67) * mm});
            skPoint(sketch, "E68.middle", {"position": v(2780.02, 1643.67) * mm});
            skLineSegment(sketch, "E69.bottom", {"start": v(2933.73, 1140.93) * mm, "end": v(2917.03, 1140.93) * mm});
            skLineSegment(sketch, "E69.top", {"start": v(2933.73, 2140.93) * mm, "end": v(2883.73, 2140.93) * mm});
            skLineSegment(sketch, "E69.left", {"start": v(2933.73, 1140.93) * mm, "end": v(2933.73, 2140.93) * mm});
            skLineSegment(sketch, "E69.right", {"start": v(2883.73, 1140.93) * mm, "end": v(2883.73, 2140.93) * mm});
            skPoint(sketch, "E69.middle", {"position": v(2908.73, 1640.93) * mm});
            skLineSegment(sketch, "E70", {"start": v(2096.82, 2554.9) * mm, "end": v(2182.85, 2554.9) * mm});
            skLineSegment(sketch, "E71.top", {"start": v(2182.85, 2492.4) * mm, "end": v(2199.45, 2492.4) * mm});
            skLineSegment(sketch, "E71.left", {"start": v(2182.85, 2554.9) * mm, "end": v(2182.85, 2492.4) * mm});
            skLineSegment(sketch, "E71.right", {"start": v(2199.45, 2554.9) * mm, "end": v(2199.45, 2492.4) * mm});
            skLineSegment(sketch, "E72.top", {"start": v(2582.58, 2492.4) * mm, "end": v(2599.18, 2492.4) * mm});
            skLineSegment(sketch, "E72.left", {"start": v(2582.58, 2554.9) * mm, "end": v(2582.58, 2492.4) * mm});
            skLineSegment(sketch, "E72.right", {"start": v(2599.18, 2554.9) * mm, "end": v(2599.18, 2492.4) * mm});
            skLineSegment(sketch, "E73.trimOffspring", {"start": v(2599.18, 2554.9) * mm, "end": v(2685.22, 2554.9) * mm});
            skLineSegment(sketch, "E74", {"start": v(2199.45, 2554.9) * mm, "end": v(2582.58, 2554.9) * mm});
            skLineSegment(sketch, "E75.trimOffspring", {"start": v(1857.78, 1983.72) * mm, "end": v(1841.08, 1983.72) * mm});
            skLineSegment(sketch, "E76.trimOffspring", {"start": v(1857.78, 2000.32) * mm, "end": v(1857.78, 2067.02) * mm});
            skLineSegment(sketch, "E77.trimOffspring", {"start": v(1857.78, 2000.32) * mm, "end": v(1841.08, 2000.32) * mm});
            skLineSegment(sketch, "E78.trimOffspring", {"start": v(1874.38, 2000.32) * mm, "end": v(1874.38, 2067.02) * mm});
            skLineSegment(sketch, "E79", {"start": v(2462.23, 1254.39) * mm, "end": v(2399.73, 1254.39) * mm});
            skLineSegment(sketch, "E80", {"start": v(2399.73, 1254.39) * mm, "end": v(2399.73, 1270.99) * mm});
            skLineSegment(sketch, "E81", {"start": v(2399.73, 1270.99) * mm, "end": v(2462.23, 1270.99) * mm});
            skLineSegment(sketch, "E82.trimOffspring", {"start": v(2462.23, 1270.99) * mm, "end": v(2462.23, 1843.04) * mm});
            skLineSegment(sketch, "E83", {"start": v(2387.23, 1243.04) * mm, "end": v(2469.85, 1243.04) * mm, "construction": true});
            skLineSegment(sketch, "E84.MirrorCS", {"start": v(2462.23, 1231.69) * mm, "end": v(2399.73, 1231.69) * mm});
            skLineSegment(sketch, "E85.MirrorCS", {"start": v(2399.73, 1231.69) * mm, "end": v(2399.73, 1215.09) * mm});
            skLineSegment(sketch, "E86.MirrorCS", {"start": v(2399.73, 1215.09) * mm, "end": v(2462.23, 1215.09) * mm});
            skLineSegment(sketch, "E87.trimOffspring", {"start": v(2462.23, 1231.69) * mm, "end": v(2462.23, 1254.39) * mm});
            skLineSegment(sketch, "E88", {"start": v(2780.02, 1643.67) * mm, "end": v(2780.02, 1354.8) * mm, "construction": true});
            skLineSegment(sketch, "E89", {"start": v(2786.16, 1643.67) * mm, "end": v(2828.68, 1643.67) * mm, "construction": true});
            skLineSegment(sketch, "E90.0", {"start": v(2771.72, 1643.67) * mm, "end": v(2771.72, 1354.8) * mm, "construction": true});
            skLineSegment(sketch, "E91.0", {"start": v(2788.32, 1643.67) * mm, "end": v(2788.32, 1354.8) * mm, "construction": true});
            skLineSegment(sketch, "E92", {"start": v(2771.72, 1643.67) * mm, "end": v(2771.72, 1143.67) * mm});
            skLineSegment(sketch, "E93", {"start": v(2771.72, 1643.67) * mm, "end": v(2788.32, 1643.67) * mm});
            skLineSegment(sketch, "E94", {"start": v(2788.32, 1643.67) * mm, "end": v(2788.32, 1143.67) * mm});
            skLineSegment(sketch, "E95.trimOffspring", {"start": v(2771.72, 1143.67) * mm, "end": v(2705.02, 1143.67) * mm});
            skLineSegment(sketch, "E96", {"start": v(2900.43, 1140.93) * mm, "end": v(2900.43, 1640.93) * mm});
            skLineSegment(sketch, "E97", {"start": v(2900.43, 1640.93) * mm, "end": v(2917.03, 1640.93) * mm});
            skLineSegment(sketch, "E98", {"start": v(2917.03, 1640.93) * mm, "end": v(2917.03, 1140.93) * mm});
            skLineSegment(sketch, "E99.trimOffspring", {"start": v(2900.43, 1140.93) * mm, "end": v(2883.73, 1140.93) * mm});
            skLineSegment(sketch, "E100", {"start": v(2705.02, 1143.67) * mm, "end": v(2705.02, 1318.67) * mm});
            skLineSegment(sketch, "E101", {"start": v(2705.02, 1318.67) * mm, "end": v(2754.72, 1318.67) * mm});
            skLineSegment(sketch, "E102", {"start": v(2754.72, 1318.67) * mm, "end": v(2754.72, 1968.67) * mm});
            skLineSegment(sketch, "E103", {"start": v(2754.72, 1968.67) * mm, "end": v(2705.02, 1968.67) * mm});
            skLineSegment(sketch, "E104", {"start": v(2705.02, 1968.67) * mm, "end": v(2705.02, 2143.67) * mm});
            skLineSegment(sketch, "E105.MirrorCS", {"start": v(2705.02, 1318.67) * mm, "end": v(2755.02, 1318.67) * mm});
            skLineSegment(sketch, "E106.MirrorCS", {"start": v(2805.32, 1318.67) * mm, "end": v(2805.32, 1968.67) * mm});
            skLineSegment(sketch, "E107.MirrorCS", {"start": v(2805.32, 1968.67) * mm, "end": v(2855.02, 1968.67) * mm});
            skLineSegment(sketch, "E108.MirrorCS", {"start": v(2855.02, 1968.67) * mm, "end": v(2855.02, 2143.67) * mm});
            skLineSegment(sketch, "E109.MirrorCS", {"start": v(2855.02, 1318.67) * mm, "end": v(2805.02, 1318.67) * mm});
            skLineSegment(sketch, "E110.MirrorCS", {"start": v(2855.02, 1143.67) * mm, "end": v(2855.02, 1318.67) * mm});
            skLineSegment(sketch, "E111.MirrorCS", {"start": v(2788.32, 1143.67) * mm, "end": v(2855.02, 1143.67) * mm});
            skLineSegment(sketch, "E112.bottom", {"start": v(3302.78, 1374.16) * mm, "end": v(3277.78, 1374.16) * mm});
            skLineSegment(sketch, "E112.top", {"start": v(3302.78, 2698.16) * mm, "end": v(3277.78, 2698.16) * mm});
            skLineSegment(sketch, "E112.left", {"start": v(3302.78, 1374.16) * mm, "end": v(3302.78, 2698.16) * mm});
            skLineSegment(sketch, "E112.right", {"start": v(3277.78, 1374.16) * mm, "end": v(3277.78, 2698.16) * mm});
            skPoint(sketch, "E112.middle", {"position": v(3290.28, 2036.16) * mm});
            skPoint(sketch, "E113.1.0.5", {"position": v(4442.76, 2103.34) * mm});
            skPoint(sketch, "E113.1.0.10", {"position": v(4442.76, 2103.34) * mm});
            skLineSegment(sketch, "E114.bottom", {"start": v(4374.27, 2145.98) * mm, "end": v(4174.27, 2145.98) * mm});
            skLineSegment(sketch, "E114.top", {"start": v(4374.27, 2195.98) * mm, "end": v(4174.27, 2195.98) * mm});
            skLineSegment(sketch, "E114.left", {"start": v(4374.27, 2145.98) * mm, "end": v(4374.27, 2195.98) * mm});
            skLineSegment(sketch, "E114.right", {"start": v(4174.27, 2145.98) * mm, "end": v(4174.27, 2195.98) * mm});
            skPoint(sketch, "E114.middle", {"position": v(4274.27, 2170.98) * mm});
            skLineSegment(sketch, "E115.bottom", {"start": v(4213.67, 2158.13) * mm, "end": v(4230.27, 2158.13) * mm});
            skLineSegment(sketch, "E115.top", {"start": v(4213.67, 2183.83) * mm, "end": v(4230.27, 2183.83) * mm});
            skLineSegment(sketch, "E115.left", {"start": v(4213.67, 2158.13) * mm, "end": v(4213.67, 2183.83) * mm});
            skLineSegment(sketch, "E115.right", {"start": v(4230.27, 2158.13) * mm, "end": v(4230.27, 2183.83) * mm});
            skPoint(sketch, "E115.middle", {"position": v(4221.97, 2170.98) * mm});
            skLineSegment(sketch, "E116.MirrorCS", {"start": v(4334.27, 2183.48) * mm, "end": v(4318.27, 2183.48) * mm});
            skLineSegment(sketch, "E117.MirrorCS", {"start": v(4334.27, 2157.78) * mm, "end": v(4334.27, 2183.48) * mm});
            skPoint(sketch, "E118.MirrorP", {"position": v(4310.27, 2170.98) * mm});
            skLineSegment(sketch, "E119.MirrorCS", {"start": v(4318.27, 2157.78) * mm, "end": v(4318.27, 2183.48) * mm});
            skLineSegment(sketch, "E120.MirrorCS", {"start": v(4334.27, 2157.78) * mm, "end": v(4318.27, 2157.78) * mm});
            skLineSegment(sketch, "E121.direction1", {"start": v(4174.27, 2145.98) * mm, "end": v(4390.37, 2145.98) * mm, "construction": true});
            skLineSegment(sketch, "E122.bottom", {"start": v(4335.27, 2027.4) * mm, "end": v(4310.27, 2027.4) * mm});
            skLineSegment(sketch, "E122.top", {"start": v(4335.27, 2127.4) * mm, "end": v(4310.27, 2127.4) * mm});
            skLineSegment(sketch, "E122.left", {"start": v(4335.27, 2027.4) * mm, "end": v(4335.27, 2127.4) * mm});
            skLineSegment(sketch, "E122.right", {"start": v(4310.27, 2027.4) * mm, "end": v(4310.27, 2127.4) * mm});
            skPoint(sketch, "E122.middle", {"position": v(4322.77, 2077.4) * mm});
            skLineSegment(sketch, "E123.bottom", {"start": v(4492.76, 2003.04) * mm, "end": v(4392.76, 2003.04) * mm});
            skLineSegment(sketch, "E123.top", {"start": v(4492.76, 2203.64) * mm, "end": v(4392.76, 2203.64) * mm});
            skLineSegment(sketch, "E123.left", {"start": v(4492.76, 2003.04) * mm, "end": v(4492.76, 2203.64) * mm});
            skLineSegment(sketch, "E123.right", {"start": v(4392.76, 2003.04) * mm, "end": v(4392.76, 2203.64) * mm});
            skLineSegment(sketch, "E124", {"start": v(4442.76, 2003.04) * mm, "end": v(4442.76, 2203.64) * mm, "construction": true});
            skLineSegment(sketch, "E125.bottom", {"start": v(4468.11, 2095) * mm, "end": v(4417.41, 2095) * mm});
            skLineSegment(sketch, "E125.top", {"start": v(4468.11, 2111.7) * mm, "end": v(4417.41, 2111.7) * mm});
            skLineSegment(sketch, "E125.left", {"start": v(4468.11, 2095) * mm, "end": v(4468.11, 2111.7) * mm});
            skLineSegment(sketch, "E125.right", {"start": v(4417.41, 2095) * mm, "end": v(4417.41, 2111.7) * mm});
            skPoint(sketch, "E126.1.0.5", {"position": v(4562.77, 2100.62) * mm});
            skPoint(sketch, "E126.1.0.10", {"position": v(4562.77, 2100.62) * mm});
            skLineSegment(sketch, "E127.bottom", {"start": v(4612.77, 2000.32) * mm, "end": v(4512.77, 2000.32) * mm});
            skLineSegment(sketch, "E127.top", {"start": v(4612.77, 2200.92) * mm, "end": v(4512.77, 2200.92) * mm});
            skLineSegment(sketch, "E127.left", {"start": v(4612.77, 2000.32) * mm, "end": v(4612.77, 2200.92) * mm});
            skLineSegment(sketch, "E127.right", {"start": v(4512.77, 2000.32) * mm, "end": v(4512.77, 2200.92) * mm});
            skLineSegment(sketch, "E128", {"start": v(4562.77, 2000.32) * mm, "end": v(4562.77, 2200.92) * mm, "construction": true});
            skLineSegment(sketch, "E129.bottom", {"start": v(4588.12, 2092.27) * mm, "end": v(4537.42, 2092.27) * mm});
            skLineSegment(sketch, "E129.top", {"start": v(4588.12, 2108.97) * mm, "end": v(4537.42, 2108.97) * mm});
            skLineSegment(sketch, "E129.left", {"start": v(4588.12, 2092.27) * mm, "end": v(4588.12, 2108.97) * mm});
            skLineSegment(sketch, "E129.right", {"start": v(4537.42, 2092.27) * mm, "end": v(4537.42, 2108.97) * mm});
            skLineSegment(sketch, "E130.bottom", {"start": v(4372.45, 2027.4) * mm, "end": v(4347.45, 2027.4) * mm});
            skLineSegment(sketch, "E130.top", {"start": v(4372.45, 2127.4) * mm, "end": v(4347.45, 2127.4) * mm});
            skLineSegment(sketch, "E130.left", {"start": v(4372.45, 2027.4) * mm, "end": v(4372.45, 2127.4) * mm});
            skLineSegment(sketch, "E130.right", {"start": v(4347.45, 2027.4) * mm, "end": v(4347.45, 2127.4) * mm});
            skPoint(sketch, "E130.middle", {"position": v(4359.95, 2077.4) * mm});
            skSolve(sketch);
        }
        {
            var Q0;
            Q0=makeQuery(id+"F1.imprint","IMPRINT",FACE,{"disambiguationData":[TD([[makeQuery(id+"F1.imprint","IMPRINT",EDGE,{"derivedFrom":sQuery(id+"F1.wireOp",EDGE,"E36.right")}),-1.0]])]});
            var Q1;
            Q1=makeQuery(id+"F1.imprint","IMPRINT",FACE,{"disambiguationData":[TD([[makeQuery(id+"F1.imprint","IMPRINT",EDGE,{"derivedFrom":sQuery(id+"F1.wireOp",EDGE,"E58.bottom")}),-1.0]])]});
            var Q2;
            Q2=makeQuery(id+"F1.imprint","IMPRINT",FACE,{"disambiguationData":[TD([[makeQuery(id+"F1.imprint","IMPRINT",EDGE,{"derivedFrom":sQuery(id+"F1.wireOp",EDGE,"E68.bottom")}),-1.0]])]});
            var Q3;
            Q3=makeQuery(id+"F1.imprint","IMPRINT",FACE,{"disambiguationData":[TD([[makeQuery(id+"F1.imprint","IMPRINT",EDGE,{"derivedFrom":sQuery(id+"F1.wireOp",EDGE,"E69.bottom")}),-1.0]])]});
            var Q4;
            Q4=makeQuery(id+"F1.imprint","IMPRINT",FACE,{"disambiguationData":[TD([[makeQuery(id+"F1.imprint","IMPRINT",EDGE,{"derivedFrom":sQuery(id+"F1.wireOp",EDGE,"E1.bottom")}),-1.0]])]});
            var Q5;
            Q5=makeQuery(id+"F1.imprint","IMPRINT",FACE,{"disambiguationData":[TD([[makeQuery(id+"F1.imprint","IMPRINT",EDGE,{"derivedFrom":sQuery(id+"F1.wireOp",EDGE,"E66.bottom")}),1.0]])]});
            extrude(context, id + "F2", {"entities" : qUnion([Q0, Q1, Q2, Q3, Q4, Q5]), "depth" : 16 * mm, "offsetDistance" : 25 * mm});
        }
        {
            var Q0;
            Q0=makeQuery(id+"F1.imprint","IMPRINT",FACE,{"disambiguationData":[TD([[makeQuery(id+"F1.imprint","IMPRINT",EDGE,{"derivedFrom":sQuery(id+"F1.wireOp",EDGE,"E68.top")}),1.0]])]});
            extrude(context, id + "F3", {"entities" : qUnion([Q0]), "depth" : (getVariable(context, 's')) * mm, "offsetDistance" : 25 * mm});
        }
        {
            var Q0;
            Q0=makeQuery(id+"F1.imprint","IMPRINT",FACE,{"disambiguationData":[TD([[makeQuery(id+"F1.imprint","IMPRINT",EDGE,{"derivedFrom":sQuery(id+"F1.wireOp",EDGE,"E112.bottom")}),-1.0]])]});
            extrude(context, id + "F4", {"entities" : qUnion([Q0]), "depth" : 16 * mm, "offsetDistance" : 25 * mm});
        }
    });
